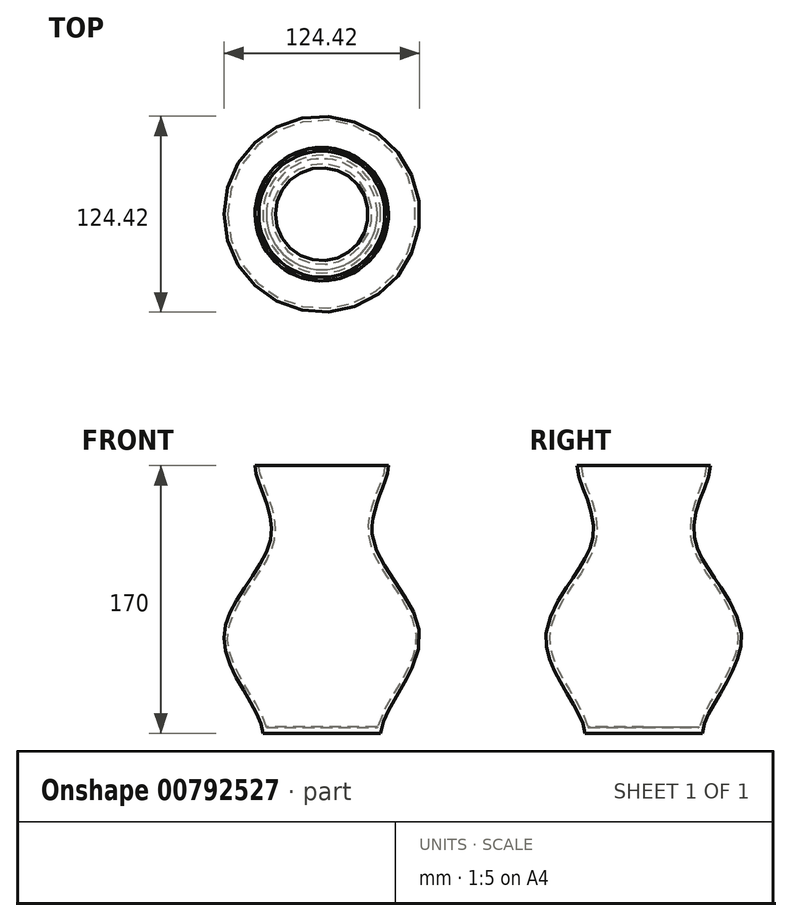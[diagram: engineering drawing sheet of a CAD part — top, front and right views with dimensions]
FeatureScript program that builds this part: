
annotation { "Feature Type Name" : "Feature", "Feature Type Description" : "" }
export const myFeature = defineFeature(function(context is Context, id is Id, definition is map)
    precondition{}
    {
        {
            var Q0;
            Q0=qCreatedBy(makeId("Top.planeOp"),FACE);
            var sketch = newSketch(context, id + "F0", { "sketchPlane" : qUnion([Q0])});
            skCircle(sketch, "E0", {"center": v(0, 0) * mm, "radius": 35.25 * mm});
            skSolve(sketch);
        }
        {
            var Q0;
            Q0=qCreatedBy(makeId("Front.planeOp"),FACE);
            var sketch = newSketch(context, id + "F1", { "sketchPlane" : qUnion([Q0])});
            skFitSpline(sketch, "E1", {"points": [v(-37.4, 0) * mm, v(-62.21, 60.31) * mm, v(-32.25, 124.85) * mm, v(-42.37, 170) * mm], "startDerivative": vector(0, 124.3) * mm, "endDerivative": vector(0, 109.2) * mm});
            skFitSpline(sketch, "E2.0", {"points": [v(-35, 0) * mm, v(-35, 1.54) * mm, v(-35.47, 4.68) * mm, v(-37.19, 9.54) * mm, v(-39.64, 14.62) * mm, v(-43.6, 21.7) * mm, v(-48.17, 29.2) * mm, v(-52.49, 36.93) * mm, v(-55.39, 42.77) * mm, v(-57.74, 48.6) * mm, v(-59.07, 53.37) * mm, v(-59.66, 57.11) * mm, v(-59.82, 59.4) * mm, v(-59.81, 61.22) * mm, v(-59.72, 63.03) * mm, v(-59.43, 65.29) * mm, v(-58.84, 68) * mm, v(-57.76, 71.63) * mm, v(-55.9, 76.17) * mm, v(-53.01, 81.63) * mm, v(-48.54, 88.93) * mm, v(-43.51, 96.24) * mm, v(-38.7, 103.6) * mm, v(-35.41, 109.16) * mm, v(-33.09, 113.87) * mm, v(-31.59, 117.68) * mm, v(-30.67, 120.58) * mm, v(-30.1, 123.03) * mm, v(-29.79, 125) * mm, v(-29.57, 126.98) * mm, v(-29.46, 129.43) * mm, v(-29.6, 133.33) * mm, v(-30.28, 138.12) * mm, v(-31.68, 143.67) * mm, v(-33.44, 149) * mm, v(-35.34, 154.06) * mm, v(-37.16, 158.78) * mm, v(-38.69, 163.1) * mm, v(-39.73, 166.94) * mm, v(-39.97, 169.07) * mm, v(-39.97, 170) * mm]});
            skLineSegment(sketch, "E3", {"start": v(-42.37, 170) * mm, "end": v(-39.97, 170) * mm});
            skLineSegment(sketch, "E4", {"start": v(-37.4, 0) * mm, "end": v(-35, 0) * mm});
            skSolve(sketch);
        }
        {
            var Q0;
            Q0=makeQuery(id+"F1.imprint","IMPRINT",FACE,{"disambiguationData":[TD([[makeQuery(id+"F1.imprint","IMPRINT",EDGE,{"derivedFrom":sQuery(id+"F1.wireOp",EDGE,"E1")}),-1.0]])]});
            var Q1;
            Q1=sQuery(id+"F0.wireOp",EDGE,"E0");
            revolve(context, id + "F2", {"surfaceOperationType" : NewSurfaceOperationType.NEW, "entities" : qUnion([Q0]), "axis" : qUnion([Q1]), "revolveType" : RevolveType.FULL});
        }
        {
            var Q0;
            Q0=makeQuery(id+"F0.imprint","IMPRINT",FACE,{"disambiguationData":[TD([[makeQuery(id+"F0.imprint","IMPRINT",EDGE,{"derivedFrom":sQuery(id+"F0.wireOp",EDGE,"E0")}),1.0]])]});
            extrude(context, id + "F3", {"entities" : qUnion([Q0]), "operationType" : NewBodyOperationType.ADD, "depth" : 4 * mm, "offsetDistance" : 25 * mm});
        }
    });
